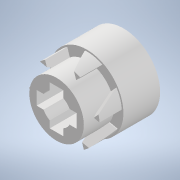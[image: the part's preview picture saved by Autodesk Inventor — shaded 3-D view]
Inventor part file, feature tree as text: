
AUTODESK INVENTOR PART (.ipt)
format: ipt  version: 2022 (Build 260153000, 153)  size: 321,536 bytes
history: native  units: mm
features: sketch x5, extrude x5, reference x5, projected_geometry x5, other x5, plane x4, chamfer x1, pattern_circular x1
ambient origin geometry x8: Origin, YZ Plane, XZ Plane, XY Plane, X Axis, Y Axis, Z Axis, Center Point
bodies: Solid1 (feature_tree)
feature tree (31):
  sketch  "Sketch1"  dims[d1=0.5mm d2=10.0mm d3=0.0mm]
  plane  "Work Plane1"
  extrude  "Extrusion1"  Depth=10.0mm TaperAngle=0.0deg
  sketch  "Sketch2"  dims[d4=0.3mm d5=10.0mm d6=0.0mm d7=2.6mm d8=2.0mm d9=11.34464mm]
  plane  "Work Plane2"
  extrude  "Extrusion2"  Depth=10.0mm TaperAngle=0.0deg
  chamfer  "Chamfer1"  Distance=2.6mm
  extrude  "Extrusion3"  Depth=1.5mm TaperAngle=360.0deg
  pattern_circular  "Circular Pattern1"  [2 undecoded]
  sketch  "Sketch4"  dims[d15=0.2mm]
  plane  "Work Plane3"
  extrude  "Extrusion4"  Depth=10.0mm
  sketch  "Sketch5"  dims[d17=10.0mm d18=0.0mm d19=0.3mm d20=0.3mm d21=10.0mm d22=0.0mm]
  plane  "Work Plane4"
  extrude  "Extrusion5"  Depth=10.0mm TaperAngle=0.0deg
  reference  "Reference1"
  reference  "Reference2"
  reference  "Reference3"
  projected_geometry  "Projected Loop1"
  sketch  "Sketch3"  dims[d10=1.5mm d11=0.0mm d12=60.0mm d13=360.0deg]
  projected_geometry  "Projected Loop2"
  reference  "Reference4"
  projected_geometry  "Projected Loop3"
  projected_geometry  "Projected Loop4"
  reference  "Reference5"
  projected_geometry  "Projected Loop5"
  other  "<userpath>\OneDrive - Imperial College London\ROBOICP\Final Assembly\Final Assembly.iam"
  other  "Final Assembly.iam"
  other  "new top 4.0:1"
  other  "male head_1.75R:1"
  other  "Mixer:1"
note: 2 required parameter values undecoded (feature->parameter linkage not recoverable at this tier; creation-order binding heuristic only, values carry confidence <= 0.55)
